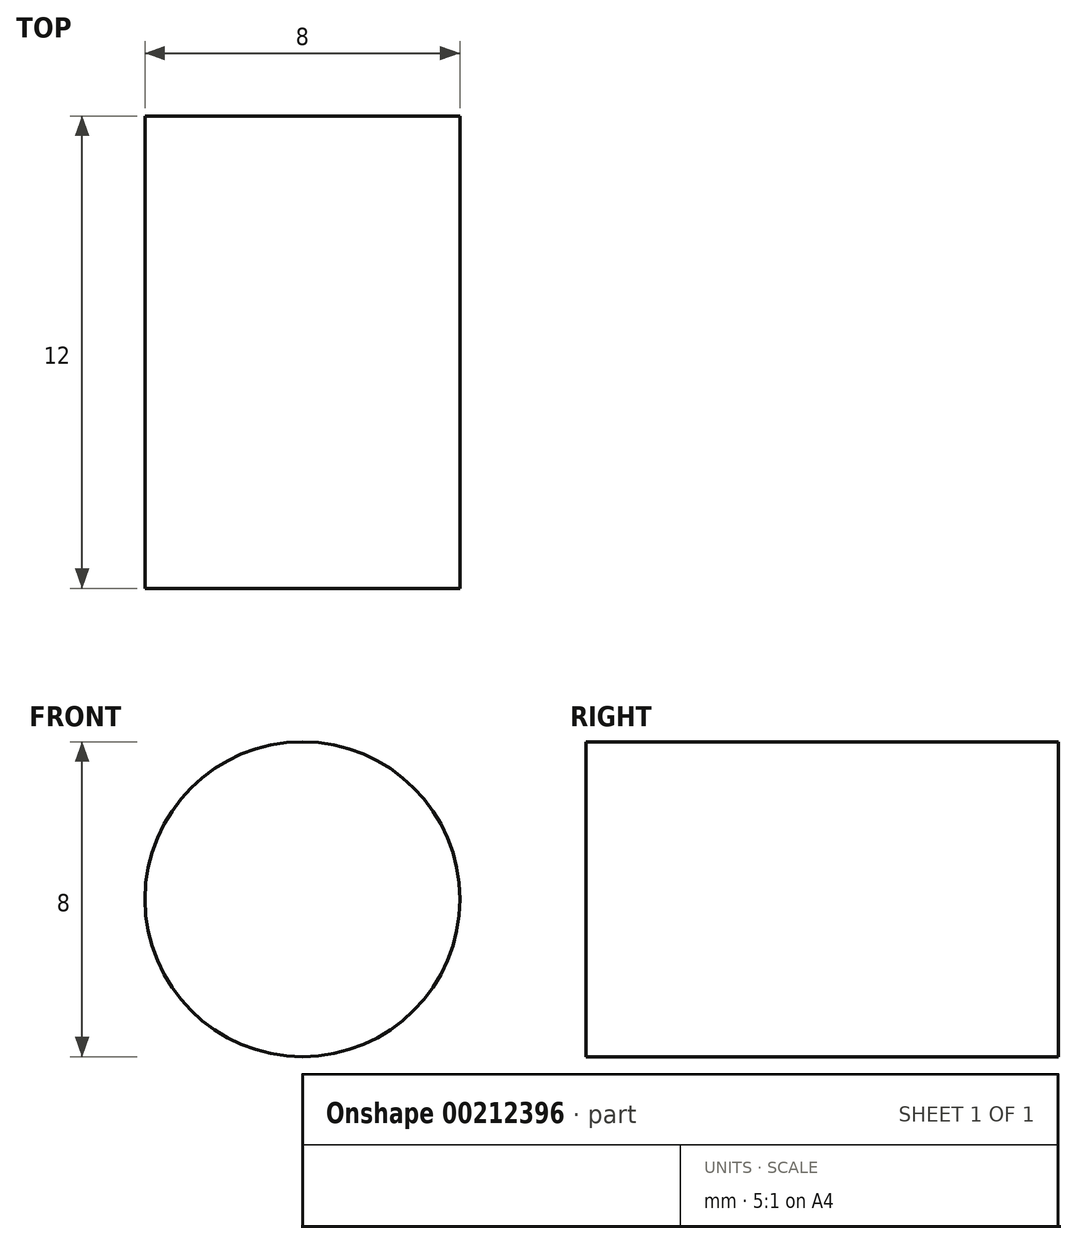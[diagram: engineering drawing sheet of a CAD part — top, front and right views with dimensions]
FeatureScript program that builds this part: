
annotation { "Feature Type Name" : "Feature", "Feature Type Description" : "" }
export const myFeature = defineFeature(function(context is Context, id is Id, definition is map)
    precondition{}
    {
        {
            var Q0;
            Q0=qCreatedBy(makeId("Front.planeOp"),FACE);
            var sketch = newSketch(context, id + "F0", { "sketchPlane" : qUnion([Q0])});
            skCircle(sketch, "E0", {"center": v(0, 0) * mm, "radius": 4 * mm});
            skSolve(sketch);
        }
        {
            var Q0;
            Q0=makeQuery(id+"F0.imprint","IMPRINT",FACE,{"disambiguationData":[TD([[makeQuery(id+"F0.imprint","IMPRINT",EDGE,{"derivedFrom":sQuery(id+"F0.wireOp",EDGE,"E0")}),1.0]])]});
            extrude(context, id + "F1", {"entities" : qUnion([Q0]), "depth" : 12 * mm});
        }
    });
